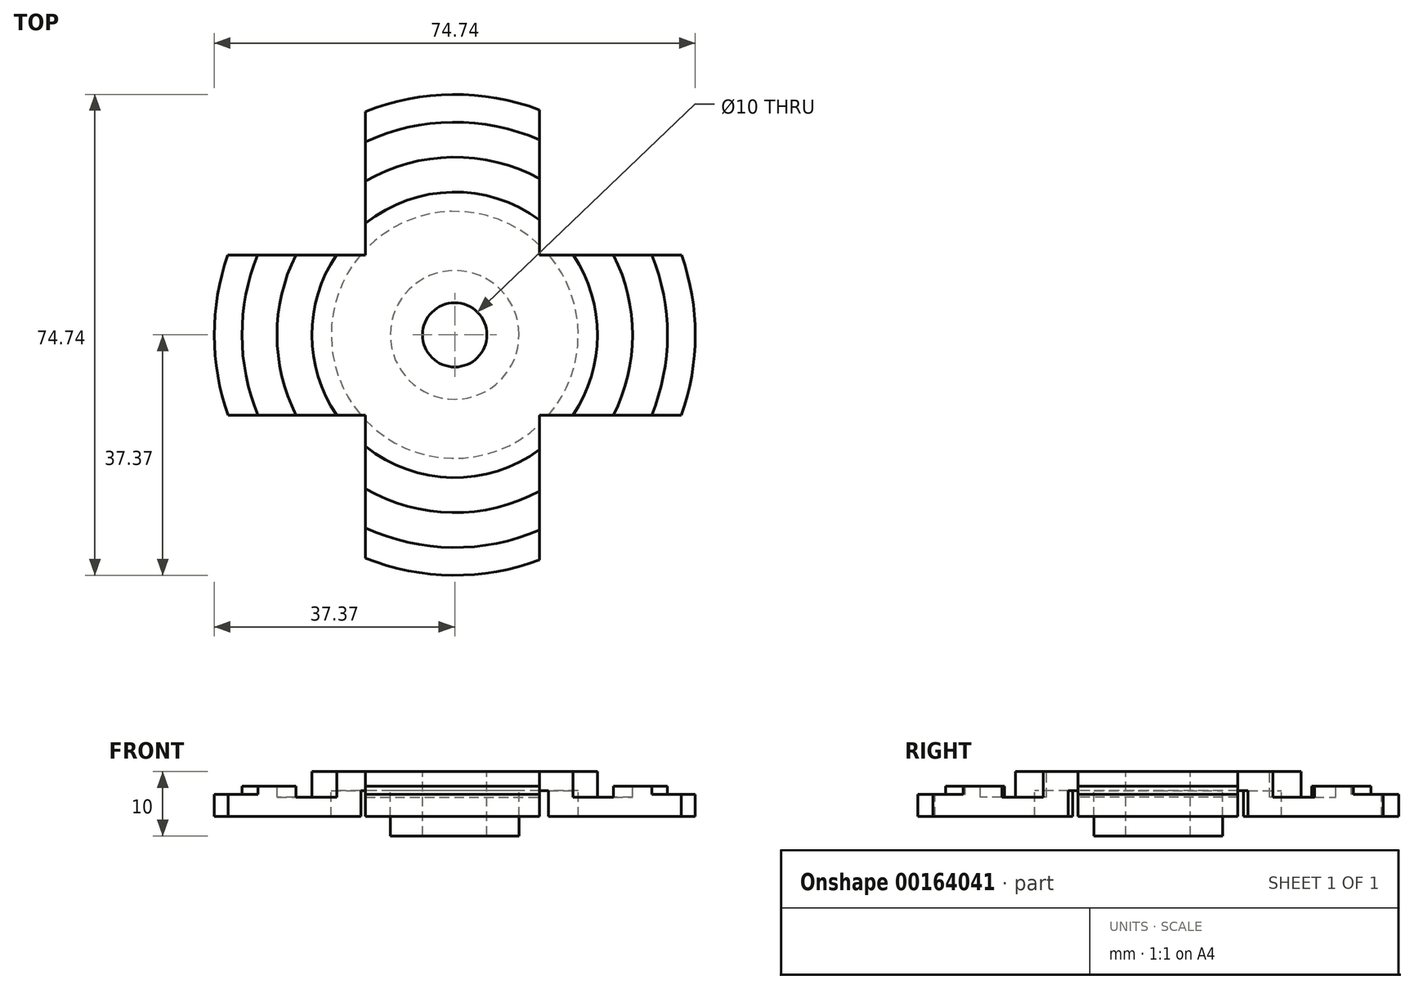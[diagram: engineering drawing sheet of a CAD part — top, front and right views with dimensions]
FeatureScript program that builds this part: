
annotation { "Feature Type Name" : "Feature", "Feature Type Description" : "" }
export const myFeature = defineFeature(function(context is Context, id is Id, definition is map)
    precondition{}
    {
        {
            var Q0;
            Q0=qCreatedBy(makeId("Front.planeOp"),FACE);
            var sketch = newSketch(context, id + "F0", { "sketchPlane" : qUnion([Q0])});
            skLineSegment(sketch, "E0.bottom", {"start": v(5, 0) * mm, "end": v(10, 0) * mm});
            skLineSegment(sketch, "E0.top", {"start": v(5, -10) * mm, "end": v(10, -10) * mm});
            skLineSegment(sketch, "E0.left", {"start": v(5, 0) * mm, "end": v(5, -10) * mm});
            skLineSegment(sketch, "E0.right", {"start": v(10, 0) * mm, "end": v(10, -10) * mm});
            skLineSegment(sketch, "E1.bottom", {"start": v(10, 0) * mm, "end": v(19.2, 0) * mm});
            skLineSegment(sketch, "E1.top", {"start": v(10, -3) * mm, "end": v(19.2, -3) * mm});
            skLineSegment(sketch, "E1.left", {"start": v(10, 0) * mm, "end": v(10, -3) * mm});
            skLineSegment(sketch, "E1.right", {"start": v(19.2, 0) * mm, "end": v(19.2, -3) * mm});
            skLineSegment(sketch, "E2.bottom", {"start": v(19.2, 0) * mm, "end": v(22.2, 0) * mm});
            skLineSegment(sketch, "E2.top", {"start": v(19.2, -7) * mm, "end": v(22.2, -7) * mm});
            skLineSegment(sketch, "E2.left", {"start": v(19.2, 0) * mm, "end": v(19.2, -7) * mm});
            skLineSegment(sketch, "E2.right", {"start": v(22.2, 0) * mm, "end": v(22.2, -7) * mm});
            skLineSegment(sketch, "E3.bottom", {"start": v(22.2, -4) * mm, "end": v(27.62, -4) * mm});
            skLineSegment(sketch, "E3.top", {"start": v(22.2, -7) * mm, "end": v(27.62, -7) * mm});
            skLineSegment(sketch, "E3.left", {"start": v(22.2, -4) * mm, "end": v(22.2, -7) * mm});
            skLineSegment(sketch, "E3.right", {"start": v(27.62, -4) * mm, "end": v(27.62, -7) * mm});
            skLineSegment(sketch, "E4.bottom", {"start": v(27.62, -2.26) * mm, "end": v(33.06, -2.26) * mm});
            skLineSegment(sketch, "E4.top", {"start": v(27.62, -7) * mm, "end": v(33.06, -7) * mm});
            skLineSegment(sketch, "E4.left", {"start": v(27.62, -2.26) * mm, "end": v(27.62, -7) * mm});
            skLineSegment(sketch, "E4.right", {"start": v(33.06, -2.26) * mm, "end": v(33.06, -7) * mm});
            skLineSegment(sketch, "E5.bottom", {"start": v(33.06, -3.52) * mm, "end": v(37.37, -3.52) * mm});
            skLineSegment(sketch, "E5.top", {"start": v(33.06, -7) * mm, "end": v(37.37, -7) * mm});
            skLineSegment(sketch, "E5.left", {"start": v(33.06, -3.52) * mm, "end": v(33.06, -7) * mm});
            skLineSegment(sketch, "E5.right", {"start": v(37.37, -3.52) * mm, "end": v(37.37, -7) * mm});
            skLineSegment(sketch, "E6", {"start": v(0, 39.92) * mm, "end": v(0, -47.01) * mm});
            skSolve(sketch);
        }
        {
            var Q0;
            Q0=makeQuery(id+"F0.imprint","IMPRINT",FACE,{"disambiguationData":[TD([[makeQuery(id+"F0.imprint","IMPRINT",EDGE,{"derivedFrom":sQuery(id+"F0.wireOp",EDGE,"E0.bottom")}),-1.0]])]});
            var Q1;
            {var subQ0=sQuery(id+"F0.wireOp",EDGE,"E1.bottom");Q1=makeQuery(id+"F0.imprint","IMPRINT",FACE,{"disambiguationData":[TD([[makeQuery(id+"F0.imprint","IMPRINT",EDGE,{"derivedFrom":subQ0}),-1.0]])]});}
            var Q2;
            {var subQ3=sQuery(id+"F0.wireOp",EDGE,"E2.bottom");Q2=makeQuery(id+"F0.imprint","IMPRINT",FACE,{"disambiguationData":[TD([[makeQuery(id+"F0.imprint","IMPRINT",EDGE,{"derivedFrom":subQ3}),-1.0]])]});}
            var Q3;
            {var subQ0=sQuery(id+"F0.wireOp",EDGE,"E3.bottom");Q3=makeQuery(id+"F0.imprint","IMPRINT",FACE,{"disambiguationData":[TD([[makeQuery(id+"F0.imprint","IMPRINT",EDGE,{"derivedFrom":subQ0}),-1.0]])]});}
            var Q4;
            {var subQ3=sQuery(id+"F0.wireOp",EDGE,"E4.bottom");Q4=makeQuery(id+"F0.imprint","IMPRINT",FACE,{"disambiguationData":[TD([[makeQuery(id+"F0.imprint","IMPRINT",EDGE,{"derivedFrom":subQ3}),-1.0]])]});}
            var Q5;
            Q5=makeQuery(id+"F0.imprint","IMPRINT",FACE,{"disambiguationData":[TD([[makeQuery(id+"F0.imprint","IMPRINT",EDGE,{"derivedFrom":sQuery(id+"F0.wireOp",EDGE,"E5.bottom")}),-1.0]])]});
            var Q6;
            Q6=sQuery(id+"F0.wireOp",EDGE,"E6");
            revolve(context, id + "F1", {"entities" : qUnion([Q0, Q1, Q2, Q3, Q4, Q5]), "axis" : qUnion([Q6]), "revolveType" : RevolveType.FULL});
        }
        {
            var Q0;
            Q0=qCreatedBy(makeId("Top.planeOp"),FACE);
            var sketch = newSketch(context, id + "F2", { "sketchPlane" : qUnion([Q0])});
            skLineSegment(sketch, "E7", {"start": v(13.18, 52.96) * mm, "end": v(13.18, 12.39) * mm});
            skLineSegment(sketch, "E8", {"start": v(-61.2, 12.39) * mm, "end": v(-13.87, 12.39) * mm});
            skLineSegment(sketch, "E9", {"start": v(-62.88, -12.48) * mm, "end": v(-13.87, -12.48) * mm});
            skLineSegment(sketch, "E10", {"start": v(-13.87, 52.96) * mm, "end": v(-13.87, 12.39) * mm});
            skLineSegment(sketch, "E11", {"start": v(-57.57, 12.39) * mm, "end": v(-57.57, -12.48) * mm});
            skLineSegment(sketch, "E12", {"start": v(53.27, 12.39) * mm, "end": v(53.27, -12.48) * mm});
            skLineSegment(sketch, "E13", {"start": v(-13.87, 40.64) * mm, "end": v(13.18, 40.64) * mm});
            skLineSegment(sketch, "E14", {"start": v(-13.87, -44.6) * mm, "end": v(13.18, -44.6) * mm});
            skLineSegment(sketch, "E15.trimOffspring", {"start": v(13.18, 12.39) * mm, "end": v(68.48, 12.39) * mm});
            skLineSegment(sketch, "E16.trimOffspring", {"start": v(-13.87, -12.48) * mm, "end": v(-13.87, -50.88) * mm});
            skLineSegment(sketch, "E17.trimOffspring", {"start": v(13.18, -12.48) * mm, "end": v(13.18, -50.88) * mm});
            skLineSegment(sketch, "E18.trimOffspring", {"start": v(13.18, -12.48) * mm, "end": v(70.4, -12.48) * mm});
            skSolve(sketch);
        }
        {
            var Q0;
            {var subQ9=sQuery(id+"F2.wireOp",EDGE,"E11");Q0=makeQuery(id+"F2.imprint","IMPRINT",FACE,{"disambiguationData":[TD([[makeQuery(id+"F2.imprint","IMPRINT",EDGE,{"derivedFrom":subQ9}),1.0]])]});}
            extrude(context, id + "F3", {"entities" : qUnion([Q0]), "operationType" : NewBodyOperationType.INTERSECT, "oppositeDirection" : true, "depth" : 22.6 * mm});
        }
    });
